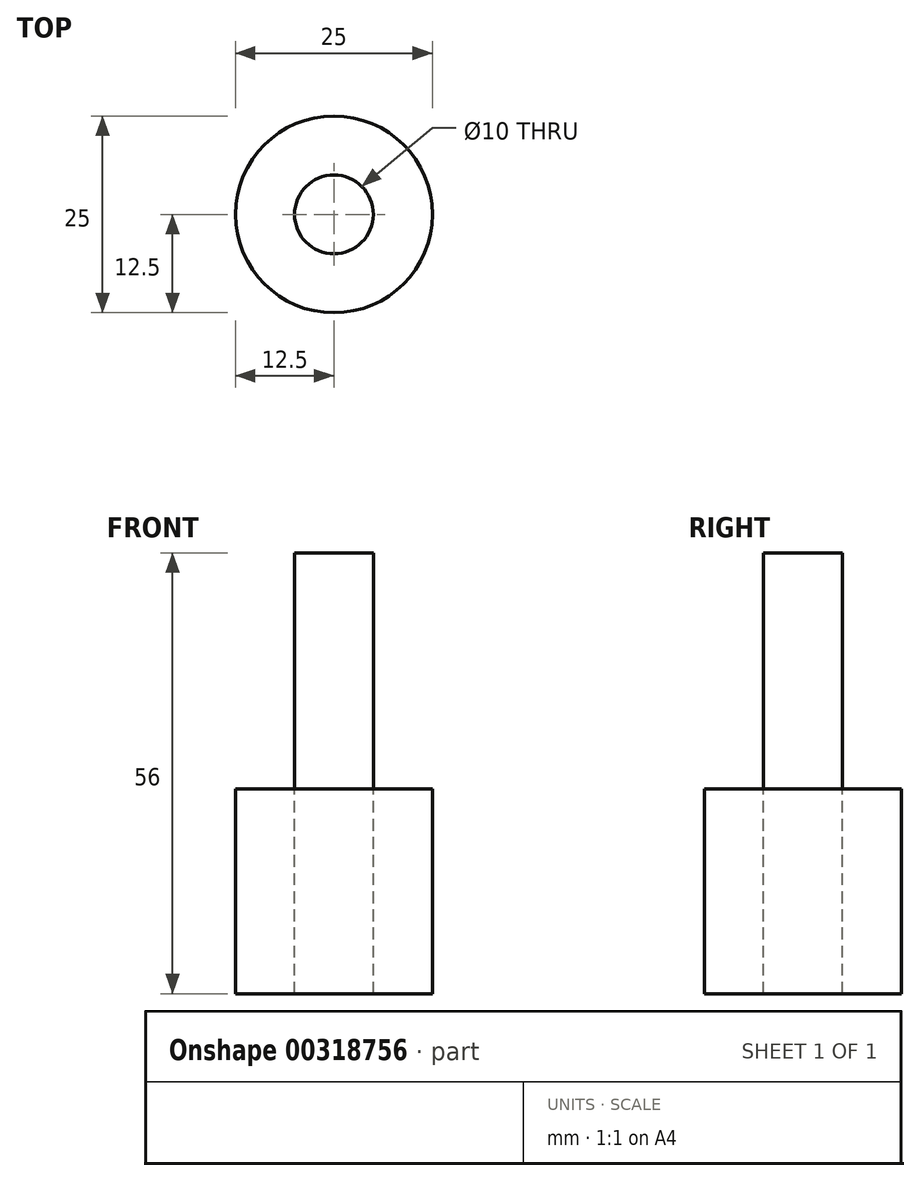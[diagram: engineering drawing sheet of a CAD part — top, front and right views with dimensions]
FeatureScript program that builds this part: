
annotation { "Feature Type Name" : "Feature", "Feature Type Description" : "" }
export const myFeature = defineFeature(function(context is Context, id is Id, definition is map)
    precondition{}
    {
        {
            var Q0;
            Q0=qCreatedBy(makeId("Top.planeOp"),FACE);
            var sketch = newSketch(context, id + "F0", { "sketchPlane" : qUnion([Q0])});
            skCircle(sketch, "E0", {"center": v(0, 0) * mm, "radius": 12.5 * mm});
            skSolve(sketch);
        }
        {
            var Q0;
            Q0=makeQuery(id+"F0.imprint","IMPRINT",FACE,{"disambiguationData":[TD([[makeQuery(id+"F0.imprint","IMPRINT",EDGE,{"derivedFrom":sQuery(id+"F0.wireOp",EDGE,"E0")}),1.0]])]});
            extrude(context, id + "F1", {"entities" : qUnion([Q0]), "depth" : 26 * mm, "offsetDistance" : 25 * mm});
        }
        {
            var Q0;
            Q0=makeQuery(id+"F1.opExtrude","CAP_FACE",FACE,{"disambiguationData":[OSD([sQuery(id+"F0.wireOp",EDGE,"E0")])],"isStart":false});
            var sketch = newSketch(context, id + "F2", { "sketchPlane" : qUnion([Q0])});
            skCircle(sketch, "E1", {"center": v(0, 0) * mm, "radius": 5 * mm});
            skSolve(sketch);
        }
        {
            var Q0;
            Q0=makeQuery(id+"F2.imprint","IMPRINT",FACE,{"disambiguationData":[TD([[makeQuery(id+"F2.imprint","IMPRINT",EDGE,{"derivedFrom":sQuery(id+"F2.wireOp",EDGE,"E1")}),1.0]])]});
            extrude(context, id + "F3", {"entities" : qUnion([Q0]), "operationType" : NewBodyOperationType.REMOVE, "oppositeDirection" : true, "depth" : 26 * mm, "offsetDistance" : 25 * mm});
        }
        {
            var Q0;
            Q0=makeQuery(id+"F1.opExtrude","CAP_FACE",FACE,{"disambiguationData":[OSD([sQuery(id+"F0.wireOp",EDGE,"E0")])],"isStart":false});
            var sketch = newSketch(context, id + "F4", { "sketchPlane" : qUnion([Q0])});
            skCircle(sketch, "E2", {"center": v(0, 0) * mm, "radius": 5 * mm});
            skSolve(sketch);
        }
        {
            var Q0;
            Q0 = qSketchRegion(id + "F4", true);
            extrude(context, id + "F5", {"entities" : qUnion([Q0]), "depth" : 30 * mm, "offsetDistance" : 25 * mm});
        }
    });
